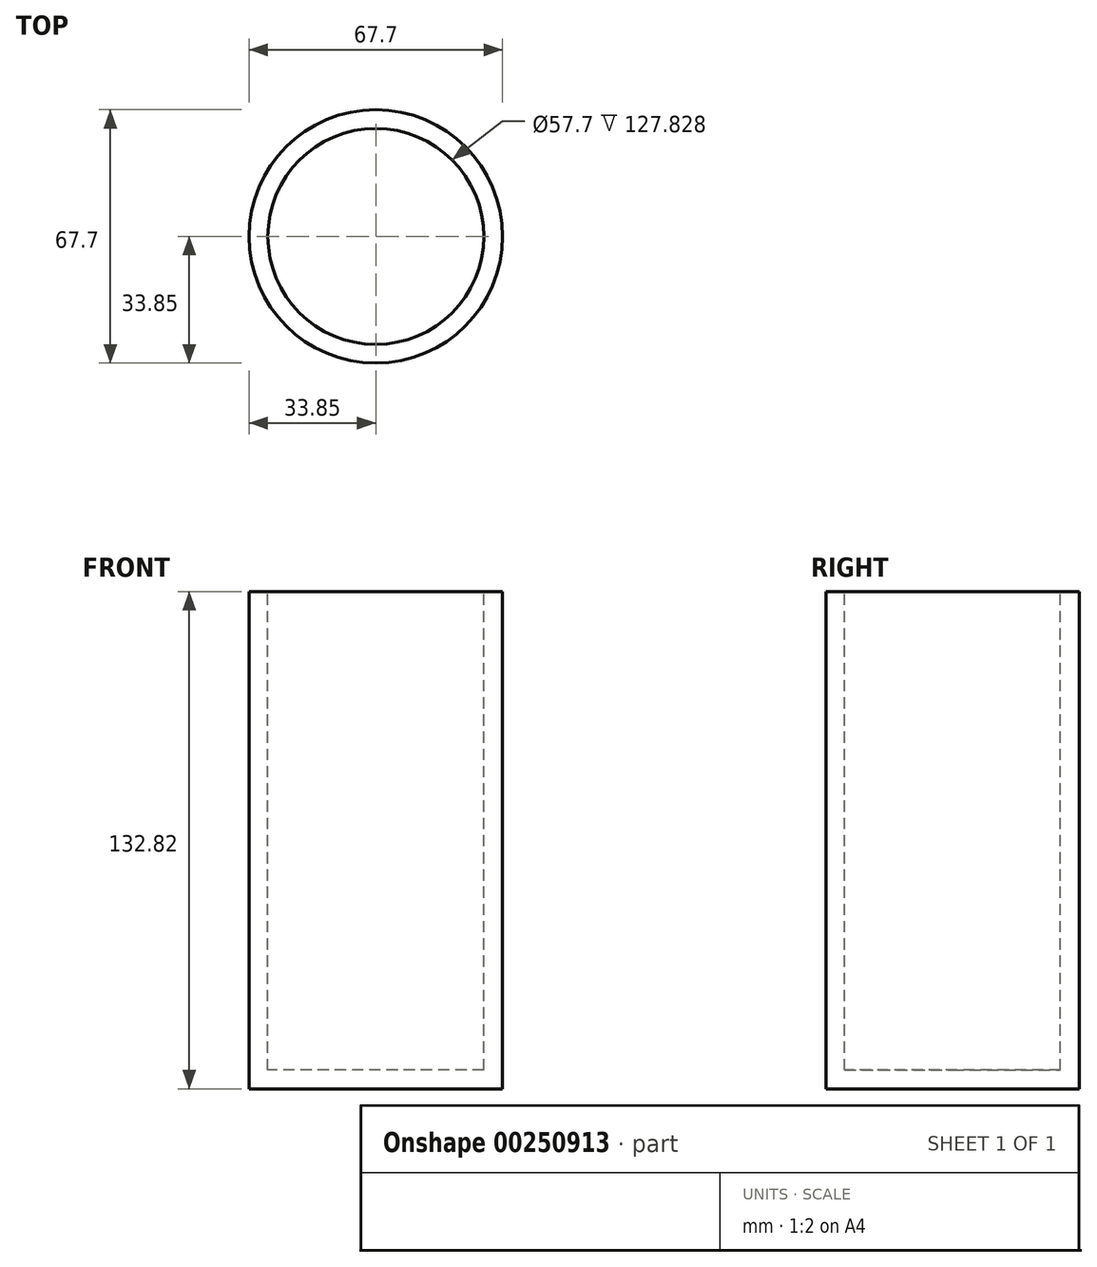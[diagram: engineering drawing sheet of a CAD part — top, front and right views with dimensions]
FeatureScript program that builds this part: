
annotation { "Feature Type Name" : "Feature", "Feature Type Description" : "" }
export const myFeature = defineFeature(function(context is Context, id is Id, definition is map)
    precondition{}
    {
        {
            var Q0;
            Q0=qCreatedBy(makeId("Front.planeOp"),FACE);
            var sketch = newSketch(context, id + "F0", { "sketchPlane" : qUnion([Q0])});
            skLineSegment(sketch, "E0.bottom", {"start": v(33.85, 66.41) * mm, "end": v(-33.85, 66.41) * mm});
            skLineSegment(sketch, "E0.top", {"start": v(33.85, -66.41) * mm, "end": v(-33.85, -66.41) * mm});
            skLineSegment(sketch, "E0.left", {"start": v(33.85, 66.41) * mm, "end": v(33.85, -66.41) * mm});
            skLineSegment(sketch, "E0.right", {"start": v(-33.85, 66.41) * mm, "end": v(-33.85, -66.41) * mm});
            skPoint(sketch, "E0.middle", {"position": v(0, 0) * mm});
            skLineSegment(sketch, "E1", {"start": v(0, 66.41) * mm, "end": v(0, -66.41) * mm});
            skSolve(sketch);
        }
        {
            var Q0;
            {var subQ0=sQuery(id+"F0.wireOp",EDGE,"E0.right");Q0=makeQuery(id+"F0.imprint","IMPRINT",FACE,{"disambiguationData":[TD([[makeQuery(id+"F0.imprint","IMPRINT",EDGE,{"derivedFrom":subQ0}),1.0]])]});}
            var Q1;
            Q1=sQuery(id+"F0.wireOp",EDGE,"E1");
            revolve(context, id + "F1", {"entities" : qUnion([Q0]), "axis" : qUnion([Q1]), "revolveType" : RevolveType.FULL});
        }
        {
            var Q0;
            Q0=makeQuery(id+"F1.opRevolve","SWEPT_FACE",FACE,{"disambiguationData":[OSD([sQuery(id+"F0.wireOp",EDGE,"E0.bottom")])]});
            shell(context, id + "F2", {"entities" : qUnion([Q0]), "thickness" : 5 * mm});
        }
    });
